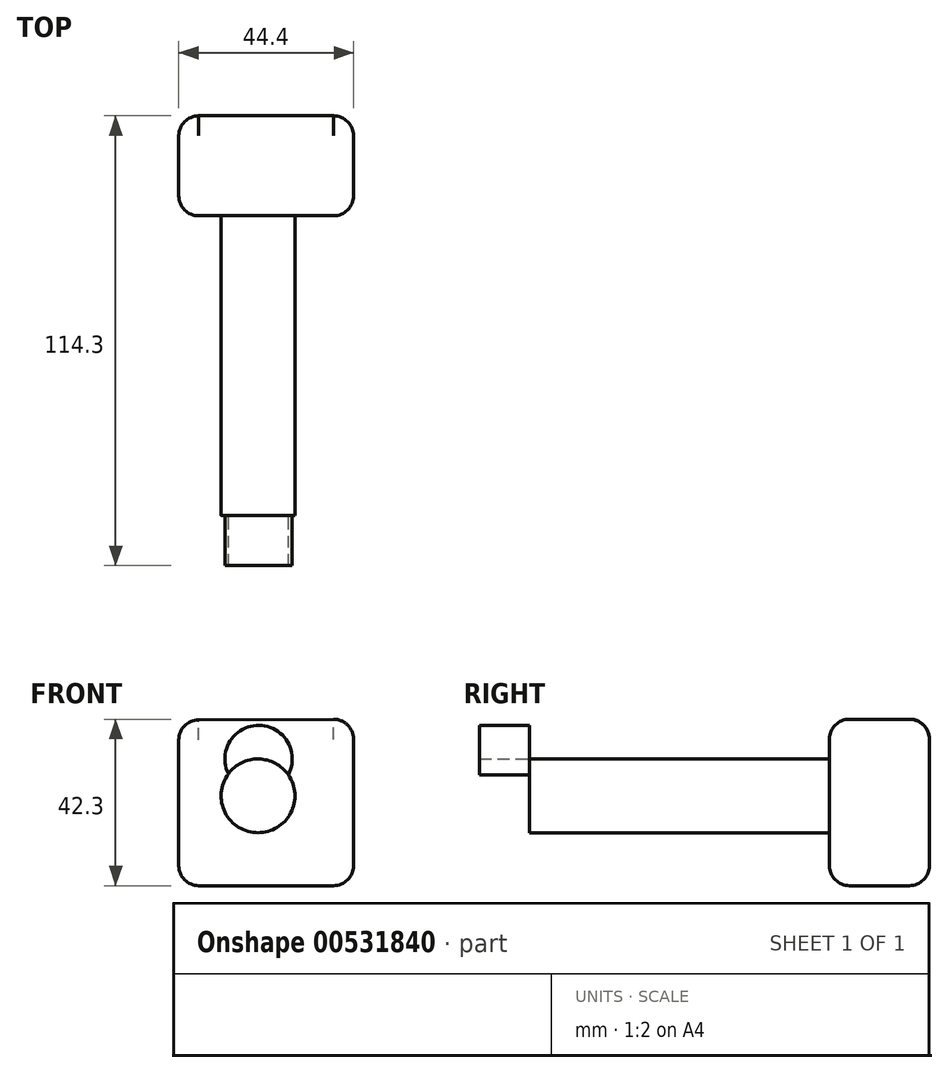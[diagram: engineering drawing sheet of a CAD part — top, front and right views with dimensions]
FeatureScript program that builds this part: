
annotation { "Feature Type Name" : "Feature", "Feature Type Description" : "" }
export const myFeature = defineFeature(function(context is Context, id is Id, definition is map)
    precondition{}
    {
        {
            var Q0;
            Q0=qCreatedBy(makeId("Front.planeOp"),FACE);
            var sketch = newSketch(context, id + "F0", { "sketchPlane" : qUnion([Q0])});
            skLineSegment(sketch, "E0", {"start": v(-44.4, 51.03) * mm, "end": v(-44.4, 8.92) * mm});
            skLineSegment(sketch, "E1", {"start": v(-44.4, 8.92) * mm, "end": v(0, 8.92) * mm});
            skLineSegment(sketch, "E2", {"start": v(0, 8.92) * mm, "end": v(0, 51.24) * mm});
            skLineSegment(sketch, "E3", {"start": v(0, 51.24) * mm, "end": v(-44.4, 51.03) * mm});
            skSolve(sketch);
        }
        {
            var Q0;
            Q0 = qSketchRegion(id + "F0", true);
            extrude(context, id + "F1", {"entities" : qUnion([Q0]), "depth" : 25.4 * mm, "offsetDistance" : 25.4 * mm});
        }
        {
            var Q0;
            Q0=makeQuery(id+"F1.opExtrude","CAP_FACE",FACE,{"disambiguationData":[OSD([sQuery(id+"F0.wireOp",EDGE,"E0"),sQuery(id+"F0.wireOp",EDGE,"E1"),sQuery(id+"F0.wireOp",EDGE,"E2"),sQuery(id+"F0.wireOp",EDGE,"E3")])],"isStart":false});
            var sketch = newSketch(context, id + "F2", { "sketchPlane" : qUnion([Q0])});
            skCircle(sketch, "E4", {"center": v(-24.27, 31.74) * mm, "radius": 9.37 * mm});
            skSolve(sketch);
        }
        {
            var Q0;
            Q0=makeQuery(id+"F2.imprint","IMPRINT",FACE,{"disambiguationData":[TD([[makeQuery(id+"F2.imprint","IMPRINT",EDGE,{"derivedFrom":sQuery(id+"F2.wireOp",EDGE,"E4")}),1.0]])]});
            extrude(context, id + "F3", {"entities" : qUnion([Q0]), "operationType" : NewBodyOperationType.ADD, "depth" : 76.2 * mm, "offsetDistance" : 25.4 * mm});
        }
        {
            var Q0;
            Q0=makeQuery(id+"F3.opExtrude","CAP_FACE",FACE,{"disambiguationData":[OSD([sQuery(id+"F2.wireOp",EDGE,"E4")])],"isStart":false});
            var sketch = newSketch(context, id + "F4", { "sketchPlane" : qUnion([Q0])});
            skCircle(sketch, "E5", {"center": v(-24.12, 41.11) * mm, "radius": 8.55 * mm});
            skSolve(sketch);
        }
        {
            var Q0;
            {var subQ0=sQuery(id+"F4.wireOp",EDGE,"E5");var subQ1=makeQuery(id+"F3.opExtrude","CAP_EDGE",EDGE,{"disambiguationData":[OSD([sQuery(id+"F2.wireOp",EDGE,"E4")])],"isStart":false});var subQ2=makeQuery(id+"F4.imprint","INTERSECT",VERTEX,{"disambiguationData":[OD(0.0)],"derivedFrom":[subQ1,subQ0]});Q0=makeQuery(id+"F4.imprint","IMPRINT",FACE,{"disambiguationData":[TD([[makeQuery(id+"F4.imprint","IMPRINT",EDGE,{"disambiguationData":[TD([[subQ2,1.0]])],"derivedFrom":subQ0}),1.0]])]});}
            extrude(context, id + "F5", {"entities" : qUnion([Q0]), "depth" : 12.7 * mm, "offsetDistance" : 25.4 * mm});
        }
        {
            var Q0;
            Q0=makeQuery(id+"F1.opExtrude","CAP_FACE",FACE,{"disambiguationData":[OSD([sQuery(id+"F0.wireOp",EDGE,"E0"),sQuery(id+"F0.wireOp",EDGE,"E1"),sQuery(id+"F0.wireOp",EDGE,"E2"),sQuery(id+"F0.wireOp",EDGE,"E3")])],"isStart":false});
            var sketch = newSketch(context, id + "F6", { "sketchPlane" : qUnion([Q0])});
            skSolve(sketch);
        }
        {
            var Q0;
            Q0=makeQuery(id+"F1.opExtrude","CAP_EDGE",EDGE,{"disambiguationData":[OSD([sQuery(id+"F0.wireOp",EDGE,"E2")])],"isStart":false});
            fillet(context, id + "F7", {"entities" : qUnion([Q0]), "radius" : 5.08 * mm, "tangentPropagation" : true, "allowEdgeOverflow" : false});
        }
        {
            var Q0;
            Q0=makeQuery(id+"F1.opExtrude","CAP_EDGE",EDGE,{"disambiguationData":[OSD([sQuery(id+"F0.wireOp",EDGE,"E2")])],"isStart":true});
            var Q1;
            Q1=makeQuery(id+"F1.opExtrude","SWEPT_FACE",FACE,{"disambiguationData":[OSD([sQuery(id+"F0.wireOp",EDGE,"E2")])]});
            fillet(context, id + "F8", {"entities" : qUnion([Q0, Q1]), "radius" : 5.08 * mm, "tangentPropagation" : true, "allowEdgeOverflow" : false});
        }
        {
            var Q0;
            Q0=makeQuery(id+"F1.opExtrude","SWEPT_EDGE",EDGE,{"disambiguationData":[OSD([sQuery(id+"F0.wireOp",EDGE,"E0"),sQuery(id+"F0.wireOp",EDGE,"E3")])]});
            var Q1;
            {var subQ0=sQuery(id+"F0.wireOp",EDGE,"E3");Q1=makeQuery(id+"F8.opFillet","BLEND_EDGE",EDGE,{"blendedFrom":[makeQuery(id+"F1.opExtrude","SWEPT_EDGE",EDGE,{"disambiguationData":[OSD([sQuery(id+"F0.wireOp",EDGE,"E2"),subQ0])]}),makeQuery(id+"F1.opExtrude","SWEPT_FACE",FACE,{"disambiguationData":[OSD([subQ0])]})],"blendedInto":[makeQuery(id+"F1.opExtrude","SWEPT_FACE",FACE,{"disambiguationData":[OSD([subQ0])]})]});}
            var Q2;
            Q2=makeQuery(id+"F1.opExtrude","CAP_EDGE",EDGE,{"disambiguationData":[OSD([sQuery(id+"F0.wireOp",EDGE,"E0")])],"isStart":true});
            var Q3;
            Q3=makeQuery(id+"F1.opExtrude","CAP_EDGE",EDGE,{"disambiguationData":[OSD([sQuery(id+"F0.wireOp",EDGE,"E0")])],"isStart":false});
            fillet(context, id + "F9", {"entities" : qUnion([Q0, Q1, Q2, Q3]), "radius" : 5.08 * mm, "tangentPropagation" : true, "allowEdgeOverflow" : false});
        }
        {
            var Q0;
            Q0=makeQuery(id+"F1.opExtrude","CAP_EDGE",EDGE,{"disambiguationData":[OSD([sQuery(id+"F0.wireOp",EDGE,"E1")])],"isStart":true});
            var Q1;
            Q1=makeQuery(id+"F1.opExtrude","CAP_EDGE",EDGE,{"disambiguationData":[OSD([sQuery(id+"F0.wireOp",EDGE,"E3")])],"isStart":true});
            fillet(context, id + "F10", {"entities" : qUnion([Q0, Q1]), "radius" : 5.08 * mm, "tangentPropagation" : true, "allowEdgeOverflow" : false});
        }
    });
